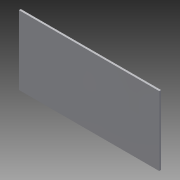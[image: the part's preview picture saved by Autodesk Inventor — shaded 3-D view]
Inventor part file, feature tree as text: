
AUTODESK INVENTOR PART (.ipt)
format: ipt  version: 2015 (Build 190159000, 159)  size: 69,632 bytes
history: native  units: mm
features: extrude x1, sketch x1
ambient origin geometry x8: Origin, YZ Plane, XZ Plane, XY Plane, X Axis, Y Axis, Z Axis, Center Point
bodies: Solid1 (feature_tree)
feature tree (2):
  extrude  "Extrusion1"  Depth=148.0mm
  sketch  "Sketch1"  dims[d0=300.0mm d1=148.0mm d2=4.0mm d3=0.0mm]
